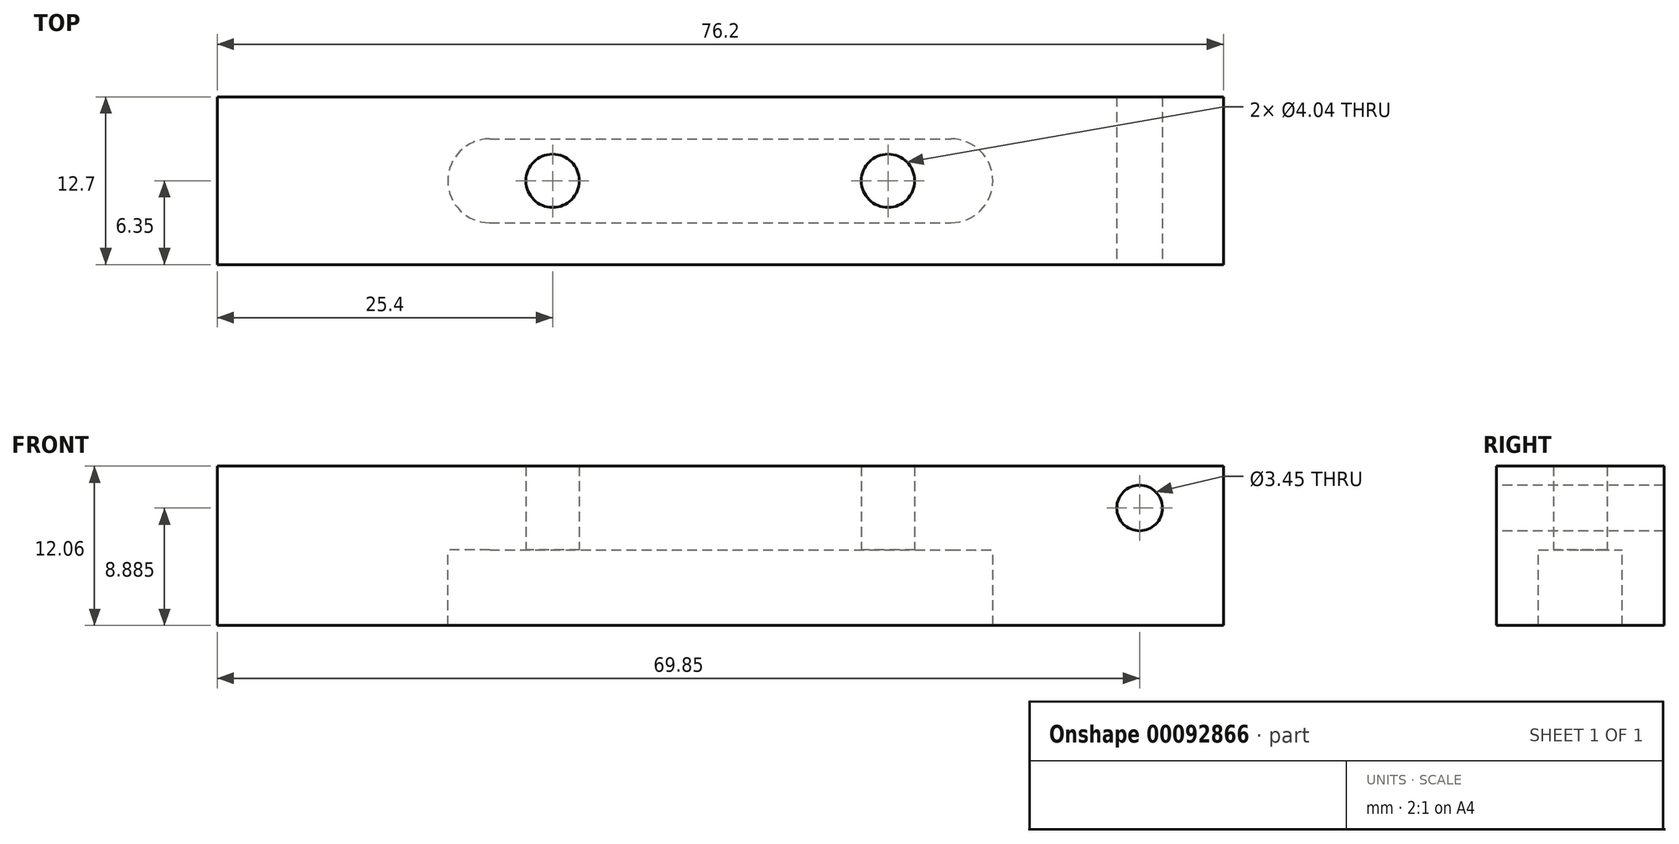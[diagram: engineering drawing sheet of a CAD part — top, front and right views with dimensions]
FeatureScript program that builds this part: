
annotation { "Feature Type Name" : "Feature", "Feature Type Description" : "" }
export const myFeature = defineFeature(function(context is Context, id is Id, definition is map)
    precondition{}
    {
        {
            var Q0;
            Q0=qCreatedBy(makeId("Top.planeOp"),FACE);
            var sketch = newSketch(context, id + "F0", { "sketchPlane" : qUnion([Q0])});
            skLineSegment(sketch, "E0.bottom", {"start": v(38.1, -6.35) * mm, "end": v(-38.1, -6.35) * mm});
            skLineSegment(sketch, "E0.top", {"start": v(38.1, 6.35) * mm, "end": v(-38.1, 6.35) * mm});
            skLineSegment(sketch, "E0.left", {"start": v(38.1, -6.35) * mm, "end": v(38.1, 6.35) * mm});
            skLineSegment(sketch, "E0.right", {"start": v(-38.1, -6.35) * mm, "end": v(-38.1, 6.35) * mm});
            skPoint(sketch, "E0.middle", {"position": v(0, 0) * mm});
            skSolve(sketch);
        }
        {
            var Q0;
            Q0=makeQuery(id+"F0.imprint","IMPRINT",FACE,{"disambiguationData":[TD([[makeQuery(id+"F0.imprint","IMPRINT",EDGE,{"derivedFrom":sQuery(id+"F0.wireOp",EDGE,"E0.bottom")}),-1.0]])]});
            extrude(context, id + "F1", {"entities" : qUnion([Q0]), "depth" : 6.35 * mm});
        }
        {
            var Q0;
            Q0=makeQuery(id+"F1.opExtrude","CAP_FACE",FACE,{"disambiguationData":[OSD([sQuery(id+"F0.wireOp",EDGE,"E0.bottom"),sQuery(id+"F0.wireOp",EDGE,"E0.top"),sQuery(id+"F0.wireOp",EDGE,"E0.left"),sQuery(id+"F0.wireOp",EDGE,"E0.right")])],"isStart":true});
            var sketch = newSketch(context, id + "F2", { "sketchPlane" : qUnion([Q0])});
            skLineSegment(sketch, "E1", {"start": v(12.7, 6.35) * mm, "end": v(12.7, -6.35) * mm, "construction": true});
            skLineSegment(sketch, "E2", {"start": v(-12.7, 6.35) * mm, "end": v(-12.7, -6.35) * mm, "construction": true});
            skPoint(sketch, "E3", {"position": v(-12.7, 0) * mm});
            skPoint(sketch, "E4", {"position": v(12.7, 0) * mm});
            skSolve(sketch);
        }
        {
            var Q0;
            Q0=makeQuery(id+"F1.opExtrude","SWEPT_FACE",FACE,{"disambiguationData":[OSD([sQuery(id+"F0.wireOp",EDGE,"E0.bottom")])]});
            var sketch = newSketch(context, id + "F3", { "sketchPlane" : qUnion([Q0])});
            skLineSegment(sketch, "E5", {"start": v(31.75, 6.35) * mm, "end": v(31.75, 0) * mm, "construction": true});
            skPoint(sketch, "E6", {"position": v(31.75, 3.18) * mm});
            skSolve(sketch);
        }
        {
            var Q0;
            Q0=sQuery(id+"F3.wireOp",VERTEX,"E6");
            var Q1;
            Q1=makeQuery(id+"F1.opExtrude","SWEPT_BODY",BODY,{"disambiguationData":[OSD([sQuery(id+"F0.wireOp",EDGE,"E0.bottom"),sQuery(id+"F0.wireOp",EDGE,"E0.top"),sQuery(id+"F0.wireOp",EDGE,"E0.left"),sQuery(id+"F0.wireOp",EDGE,"E0.right")])]});
            hole(context, id + "F4", {"style" : HoleStyle.SIMPLE, "endStyle" : HoleEndStyle.THROUGH, "standardTappedOrClearance" : lookupTablePath({ "standard" : "ANSI", "engagement" : "75%", "pitch" : "32 tpi", "size" : "#8", "type" : "Tapped" }), "standardBlindInLast" : lookupTablePath({ "standard" : "ANSI", "engagement" : "75%", "pitch" : "32 tpi", "size" : "#8", "type" : "Tapped" }), "holeDiameter" : 3.45 * mm, "startFromSketch" : true, "locations" : qUnion([Q0]), "scope" : qUnion([Q1]), "isTappedThrough" : true, "majorDiameter" : 4.17 * mm, "showTappedDepth" : true});
        }
        {
            var Q0;
            Q0=makeQuery(id+"F2.imprint","IMPRINT",FACE,{"disambiguationData":[TD([[makeQuery(id+"F2.imprint","IMPRINT",EDGE,{"derivedFrom":makeQuery(id+"F1.opExtrude","CAP_EDGE",EDGE,{"disambiguationData":[OSD([sQuery(id+"F0.wireOp",EDGE,"E0.bottom")])],"isStart":true})}),1.0]])]});
            var sketch = newSketch(context, id + "F5", { "sketchPlane" : qUnion([Q0])});
            skLineSegment(sketch, "E7.0.0", {"start": v(38.1, 6.35) * mm, "end": v(-38.1, 6.35) * mm, "construction": true});
            skLineSegment(sketch, "E7.0.1", {"start": v(-38.1, 6.35) * mm, "end": v(-38.1, -6.35) * mm, "construction": true});
            skLineSegment(sketch, "E7.0.2", {"start": v(-38.1, -6.35) * mm, "end": v(38.1, -6.35) * mm, "construction": true});
            skLineSegment(sketch, "E7.0.3", {"start": v(38.1, -6.35) * mm, "end": v(38.1, 6.35) * mm, "construction": true});
            skLineSegment(sketch, "E8", {"start": v(0, 6.35) * mm, "end": v(0, -6.35) * mm, "construction": true});
            skLineSegment(sketch, "E9", {"start": v(17.46, 6.35) * mm, "end": v(17.46, -6.35) * mm, "construction": true});
            skLineSegment(sketch, "E10", {"start": v(-17.46, 6.35) * mm, "end": v(-17.46, -6.35) * mm, "construction": true});
            skLineSegment(sketch, "E11", {"start": v(-17.46, 0) * mm, "end": v(17.46, 0) * mm, "construction": true});
            skArc(sketch, "E12.0.startCap", {"start": v(-17.46, -3.18) * mm, "mid": v(-20.64, 0) * mm, "end": v(-17.46, 3.17) * mm});
            skArc(sketch, "E12.0.endCap", {"start": v(17.46, 3.17) * mm, "mid": v(20.64, 0) * mm, "end": v(17.46, -3.18) * mm});
            skLineSegment(sketch, "E12.0.left", {"start": v(-17.46, 3.17) * mm, "end": v(17.46, 3.17) * mm});
            skLineSegment(sketch, "E12.0.right", {"start": v(-17.46, -3.18) * mm, "end": v(17.46, -3.18) * mm});
            skPoint(sketch, "E13.0", {"position": v(-12.7, 0) * mm});
            skPoint(sketch, "E14.0", {"position": v(12.7, 0) * mm});
            skSolve(sketch);
        }
        {
            var Q0;
            Q0=makeQuery(id+"F5.imprint","IMPRINT",FACE,{"disambiguationData":[TD([[makeQuery(id+"F5.imprint","IMPRINT",EDGE,{"derivedFrom":sQuery(id+"F5.wireOp",EDGE,"E12.0.startCap")}),-1.0]])]});
            extrude(context, id + "F6", {"entities" : qUnion([Q0]), "operationType" : NewBodyOperationType.ADD, "depth" : 5.7 * mm});
        }
        {
            var Q0;
            Q0=makeQuery(id+"F6.opExtrude","CAP_FACE",FACE,{"disambiguationData":[OSD([sQuery(id+"F5.wireOp",EDGE,"E12.0.startCap"),sQuery(id+"F5.wireOp",EDGE,"E12.0.endCap"),sQuery(id+"F5.wireOp",EDGE,"E12.0.left"),sQuery(id+"F5.wireOp",EDGE,"E12.0.right")])],"isStart":false});
            var sketch = newSketch(context, id + "F7", { "sketchPlane" : qUnion([Q0])});
            skPoint(sketch, "E15.0", {"position": v(-12.7, 0) * mm});
            skPoint(sketch, "E16.0", {"position": v(12.7, 0) * mm});
            skSolve(sketch);
        }
        {
            var Q0;
            Q0=sQuery(id+"F7.wireOp",VERTEX,"E15.0");
            var Q1;
            Q1=sQuery(id+"F7.wireOp",VERTEX,"E16.0");
            var Q2;
            Q2=makeQuery(id+"F1.opExtrude","SWEPT_BODY",BODY,{"disambiguationData":[OSD([sQuery(id+"F0.wireOp",EDGE,"E0.bottom"),sQuery(id+"F0.wireOp",EDGE,"E0.top"),sQuery(id+"F0.wireOp",EDGE,"E0.left"),sQuery(id+"F0.wireOp",EDGE,"E0.right")])]});
            hole(context, id + "F8", {"style" : HoleStyle.SIMPLE, "endStyle" : HoleEndStyle.BLIND, "standardTappedOrClearance" : lookupTablePath({ "standard" : "ANSI", "engagement" : "75%", "pitch" : "32 tpi", "size" : "#10", "type" : "Tapped" }), "standardBlindInLast" : lookupTablePath({ "standard" : "ANSI", "engagement" : "75%", "pitch" : "32 tpi", "size" : "#10", "type" : "Tapped" }), "holeDiameter" : 4.04 * mm, "holeDepth" : 10.16 * mm, "locations" : qUnion([Q0, Q1]), "scope" : qUnion([Q2]), "majorDiameter" : 4.83 * mm});
        }
    });
